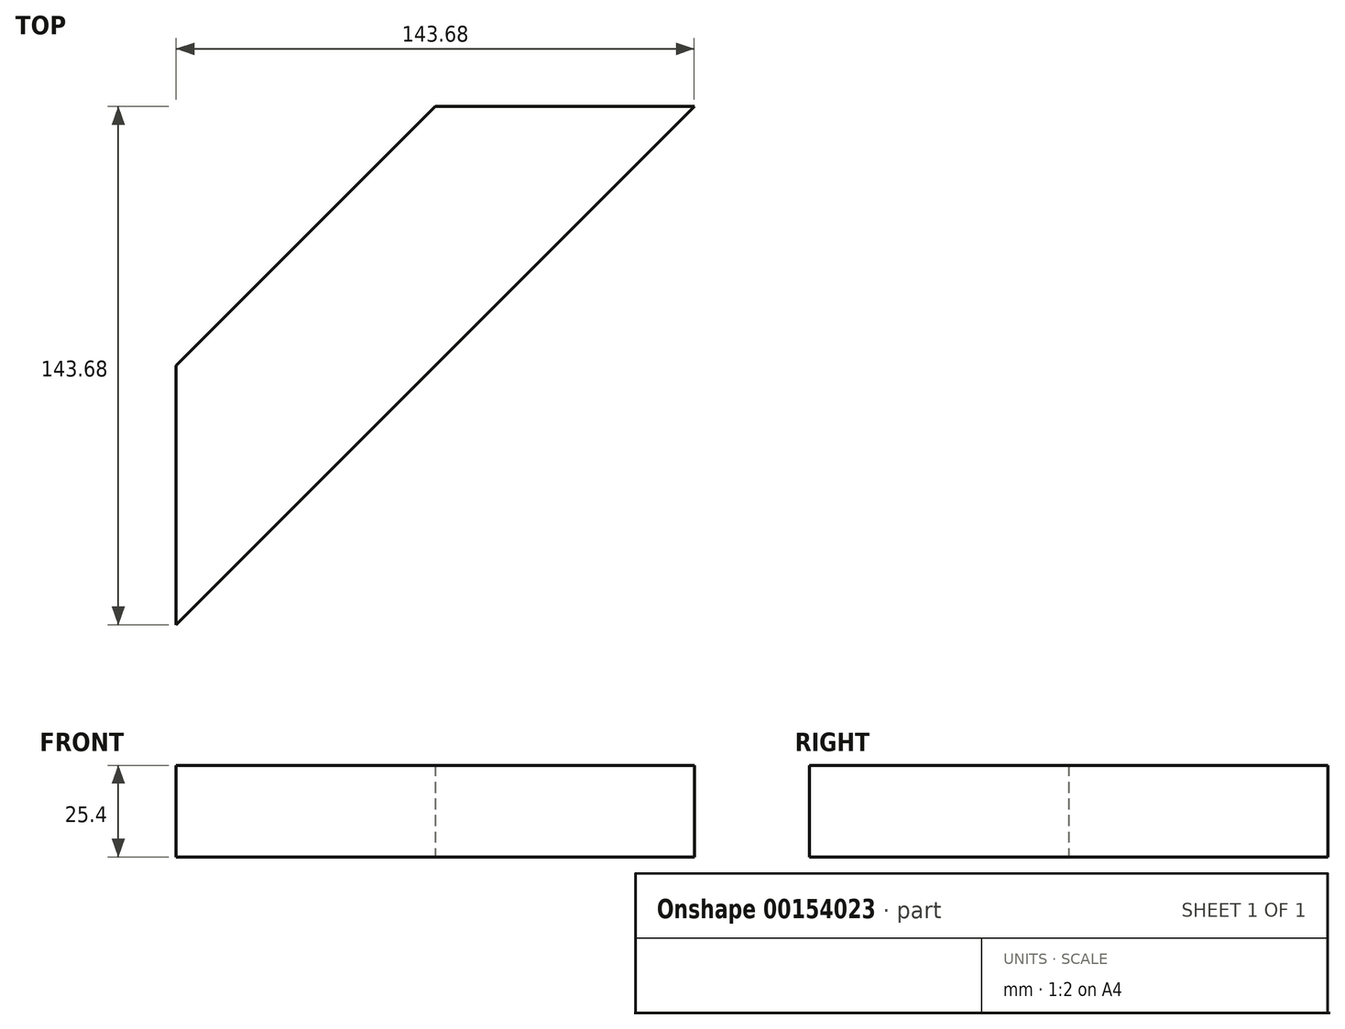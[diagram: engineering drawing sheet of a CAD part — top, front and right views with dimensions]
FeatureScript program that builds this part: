
annotation { "Feature Type Name" : "Feature", "Feature Type Description" : "" }
export const myFeature = defineFeature(function(context is Context, id is Id, definition is map)
    precondition{}
    {
        {
            var Q0;
            Q0=qCreatedBy(makeId("Top.planeOp"),FACE);
            var sketch = newSketch(context, id + "F0", { "sketchPlane" : qUnion([Q0])});
            skLineSegment(sketch, "E0", {"start": v(0, 0) * mm, "end": v(0, -143.68) * mm, "construction": true});
            skLineSegment(sketch, "E1", {"start": v(0, -143.68) * mm, "end": v(143.68, 0) * mm});
            skLineSegment(sketch, "E2", {"start": v(143.68, 0) * mm, "end": v(0, 0) * mm, "construction": true});
            skLineSegment(sketch, "E3", {"start": v(0, -71.84) * mm, "end": v(71.84, 0) * mm});
            skPoint(sketch, "E4", {"position": v(0, 0) * mm});
            skLineSegment(sketch, "E5", {"start": v(0, -143.68) * mm, "end": v(0, -71.84) * mm});
            skLineSegment(sketch, "E6", {"start": v(143.68, 0) * mm, "end": v(71.84, 0) * mm, "construction": true});
            skLineSegment(sketch, "E7", {"start": v(143.68, 0) * mm, "end": v(71.84, 0) * mm});
            skSolve(sketch);
        }
        {
            var Q0;
            Q0 = qSketchRegion(id + "F0", true);
            extrude(context, id + "F1", {"entities" : qUnion([Q0]), "depth" : 25.4 * mm});
        }
    });
